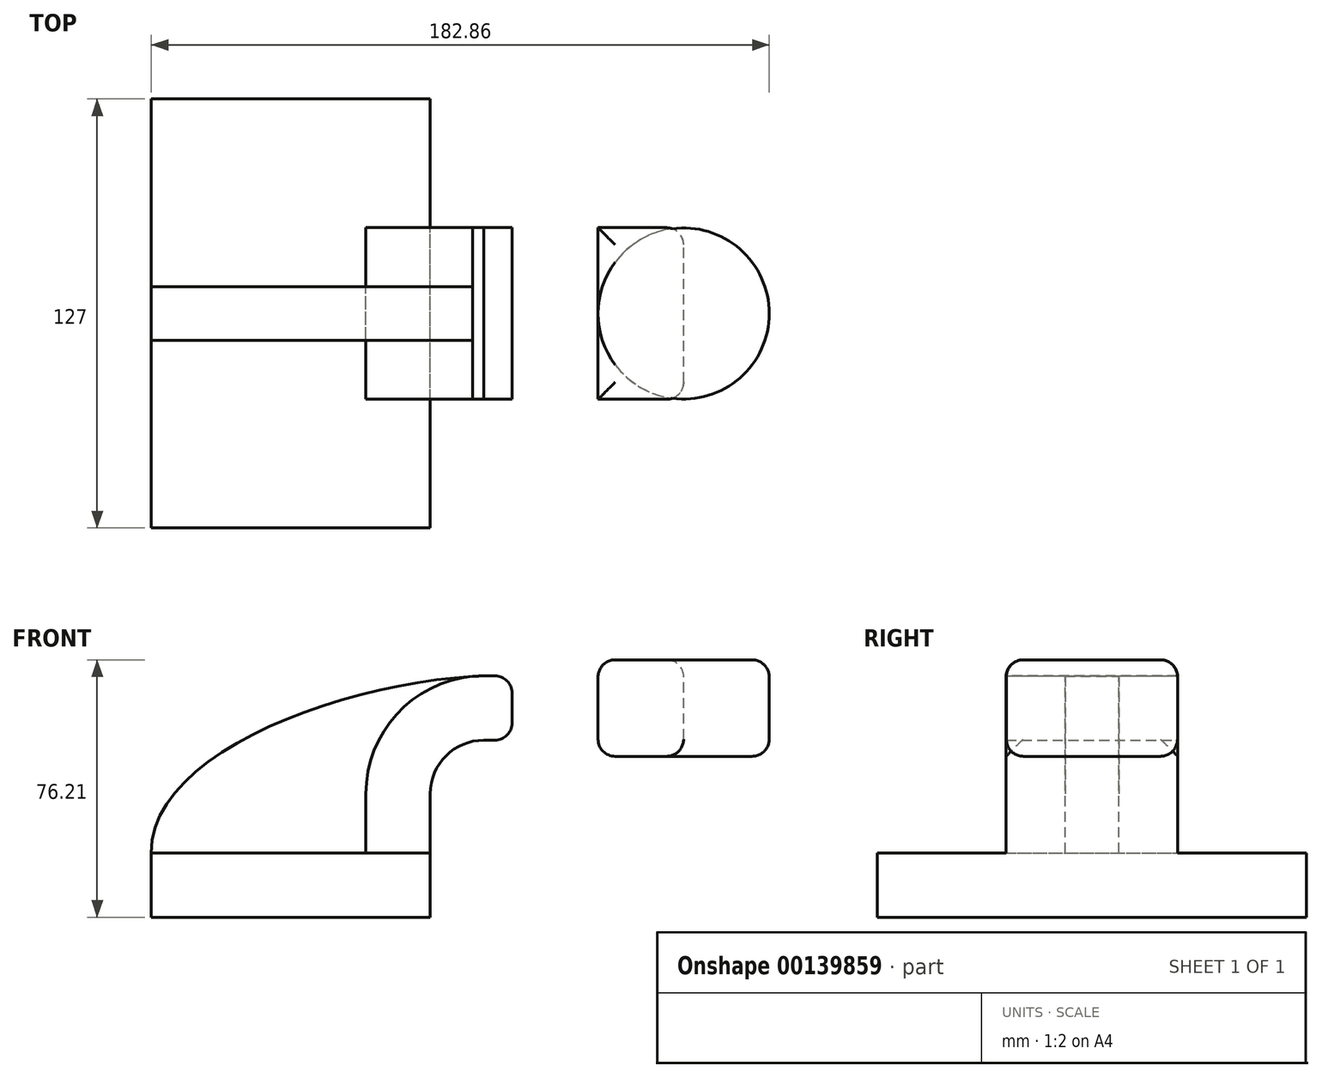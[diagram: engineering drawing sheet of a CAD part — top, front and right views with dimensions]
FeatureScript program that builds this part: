
annotation { "Feature Type Name" : "Feature", "Feature Type Description" : "" }
export const myFeature = defineFeature(function(context is Context, id is Id, definition is map)
    precondition{}
    {
        {
            var Q0;
            Q0=qCreatedBy(makeId("Front.planeOp"),FACE);
            var sketch = newSketch(context, id + "F0", { "sketchPlane" : qUnion([Q0])});
            skLineSegment(sketch, "E0.bottom", {"start": v(41.28, -9.52) * mm, "end": v(-41.28, -9.53) * mm});
            skLineSegment(sketch, "E0.top", {"start": v(41.28, 9.53) * mm, "end": v(-41.28, 9.53) * mm});
            skLineSegment(sketch, "E0.left", {"start": v(41.28, -9.52) * mm, "end": v(41.28, 9.53) * mm});
            skLineSegment(sketch, "E0.right", {"start": v(-41.28, -9.52) * mm, "end": v(-41.28, 9.53) * mm});
            skPoint(sketch, "E0.middle", {"position": v(0, 0) * mm});
            skLineSegment(sketch, "E1.bottom", {"start": v(65.46, 38.1) * mm, "end": v(116.26, 38.1) * mm});
            skLineSegment(sketch, "E1.top", {"start": v(65.46, 66.68) * mm, "end": v(116.26, 66.68) * mm});
            skLineSegment(sketch, "E1.left", {"start": v(65.46, 38.1) * mm, "end": v(65.46, 66.68) * mm});
            skLineSegment(sketch, "E1.right", {"start": v(116.26, 38.1) * mm, "end": v(116.26, 66.68) * mm});
            skPoint(sketch, "E1.middle", {"position": v(90.86, 52.39) * mm});
            skLineSegment(sketch, "E2", {"start": v(41.28, 9.53) * mm, "end": v(41.28, 27) * mm});
            skArc(sketch, "E3", {"start": v(41.27, 27) * mm, "mid": v(45.92, 38.23) * mm, "end": v(57.15, 42.88) * mm});
            skLineSegment(sketch, "E4", {"start": v(57.15, 42.88) * mm, "end": v(65.46, 42.88) * mm});
            skLineSegment(sketch, "E5.0", {"start": v(57.15, 61.93) * mm, "end": v(65.46, 61.93) * mm});
            skArc(sketch, "E5.1", {"start": v(22.23, 27) * mm, "mid": v(32.45, 51.7) * mm, "end": v(57.15, 61.93) * mm});
            skLineSegment(sketch, "E5.2", {"start": v(22.23, 9.53) * mm, "end": v(22.23, 27) * mm});
            skLineSegment(sketch, "E6", {"start": v(65.46, 61.93) * mm, "end": v(65.46, 42.88) * mm});
            skFitSpline(sketch, "E7", {"points": [v(-41.28, 9.53) * mm, v(57.15, 61.93) * mm], "startDerivative": vector(-1.47, 90.2) * mm, "endDerivative": vector(119.81, 4.21) * mm});
            skLineSegment(sketch, "E8", {"start": v(90.93, 38.1) * mm, "end": v(90.93, 66.68) * mm});
            skSolve(sketch);
        }
        {
            var Q0;
            Q0=makeQuery(id+"F0.imprint","IMPRINT",FACE,{"disambiguationData":[TD([[makeQuery(id+"F0.imprint","IMPRINT",EDGE,{"derivedFrom":sQuery(id+"F0.wireOp",EDGE,"E0.bottom")}),-1.0]])]});
            extrude(context, id + "F1", {"entities" : qUnion([Q0]), "endBound" : BoundingType.SYMMETRIC, "depth" : 127 * mm});
        }
        {
            var Q0;
            {var subQ1=sQuery(id+"F0.wireOp",EDGE,"E2");Q0=makeQuery(id+"F0.imprint","IMPRINT",FACE,{"disambiguationData":[TD([[makeQuery(id+"F0.imprint","IMPRINT",EDGE,{"derivedFrom":subQ1}),1.0]])]});}
            var Q1;
            {var subQ3=sQuery(id+"F0.wireOp",EDGE,"E1.bottom");Q1=makeQuery(id+"F0.imprint","IMPRINT",FACE,{"disambiguationData":[TD([[makeQuery(id+"F0.imprint","IMPRINT",EDGE,{"derivedFrom":subQ3}),1.0]])]});}
            var Q2;
            {var subQ5=sQuery(id+"F0.wireOp",EDGE,"kciUwsg2-KRQE-zI7N-wxgR-Qbvun73c1qAJ");Q2=makeQuery(id+"F0.imprint","IMPRINT",FACE,{"disambiguationData":[TD([[makeQuery(id+"F0.imprint","IMPRINT",EDGE,{"derivedFrom":subQ5}),1.0]])]});}
            var Q3;
            Q3=makeQuery(id+"F0.imprint","IMPRINT",FACE,{"disambiguationData":[TD([[makeQuery(id+"F0.imprint","IMPRINT",EDGE,{"derivedFrom":sQuery(id+"F0.wireOp",EDGE,"E6")}),1.0]])]});
            var Q4;
            {var subQ0=sQuery(id+"F0.wireOp",EDGE,"E1.right");Q4=makeQuery(id+"F0.imprint","IMPRINT",FACE,{"disambiguationData":[TD([[makeQuery(id+"F0.imprint","IMPRINT",EDGE,{"derivedFrom":subQ0}),1.0]])]});}
            extrude(context, id + "F2", {"entities" : qUnion([Q0, Q1, Q2, Q3, Q4]), "operationType" : NewBodyOperationType.ADD, "endBound" : BoundingType.SYMMETRIC, "depth" : 50.8 * mm});
        }
        {
            var Q0;
            {var subQ3=sQuery(id+"F0.wireOp",EDGE,"E5.2");Q0=makeQuery(id+"F0.imprint","IMPRINT",FACE,{"disambiguationData":[TD([[makeQuery(id+"F0.imprint","IMPRINT",EDGE,{"derivedFrom":subQ3}),1.0]])]});}
            extrude(context, id + "F3", {"entities" : qUnion([Q0]), "endBound" : BoundingType.SYMMETRIC, "depth" : 15.88 * mm});
        }
        {
            var Q0;
            {var subQ0=sQuery(id+"F0.wireOp",EDGE,"E1.right");Q0=makeQuery(id+"F0.imprint","IMPRINT",FACE,{"disambiguationData":[TD([[makeQuery(id+"F0.imprint","IMPRINT",EDGE,{"derivedFrom":subQ0}),1.0]])]});}
            var Q1;
            Q1=sQuery(id+"F0.wireOp",EDGE,"E1.right");
            revolve(context, id + "F4", {"entities" : qUnion([Q0]), "axis" : qUnion([Q1]), "revolveType" : RevolveType.FULL});
        }
        {
            var Q0;
            Q0=makeQuery(id+"F4.opRevolve","SWEPT_EDGE",EDGE,{"disambiguationData":[OSD([sQuery(id+"F0.wireOp",EDGE,"E1.bottom"),sQuery(id+"F0.wireOp",EDGE,"E8")])]});
            var Q1;
            Q1=makeQuery(id+"F4.opRevolve","SWEPT_EDGE",EDGE,{"disambiguationData":[OSD([sQuery(id+"F0.wireOp",EDGE,"E1.top"),sQuery(id+"F0.wireOp",EDGE,"E8")])]});
            var Q2;
            Q2=makeQuery(id+"F2.opExtrude","CAP_EDGE",EDGE,{"disambiguationData":[OSD([sQuery(id+"F0.wireOp",EDGE,"E1.top")])],"isStart":true});
            var Q3;
            Q3=makeQuery(id+"F2.opExtrude","CAP_EDGE",EDGE,{"disambiguationData":[OSD([sQuery(id+"F0.wireOp",EDGE,"E1.top")])],"isStart":false});
            var Q4;
            Q4=makeQuery(id+"F2.opExtrude","SWEPT_EDGE",EDGE,{"disambiguationData":[OSD([sQuery(id+"F0.wireOp",EDGE,"E1.bottom"),sQuery(id+"F0.wireOp",EDGE,"E1.left")])]});
            var Q5;
            Q5=makeQuery(id+"F2.opExtrude","SWEPT_EDGE",EDGE,{"disambiguationData":[OSD([sQuery(id+"F0.wireOp",EDGE,"E1.top"),sQuery(id+"F0.wireOp",EDGE,"E1.left")])]});
            var Q6;
            Q6=makeQuery(id+"F2.opExtrude","CAP_EDGE",EDGE,{"disambiguationData":[OSD([sQuery(id+"F0.wireOp",EDGE,"E1.right")])],"isStart":false});
            var Q7;
            Q7=makeQuery(id+"F2.opExtrude","CAP_EDGE",EDGE,{"disambiguationData":[OSD([sQuery(id+"F0.wireOp",EDGE,"E1.right")])],"isStart":true});
            fillet(context, id + "F5", {"entities" : qUnion([Q0, Q1, Q2, Q3, Q4, Q5, Q6, Q7]), "radius" : 5.08 * mm, "tangentPropagation" : true, "allowEdgeOverflow" : false});
        }
    });
